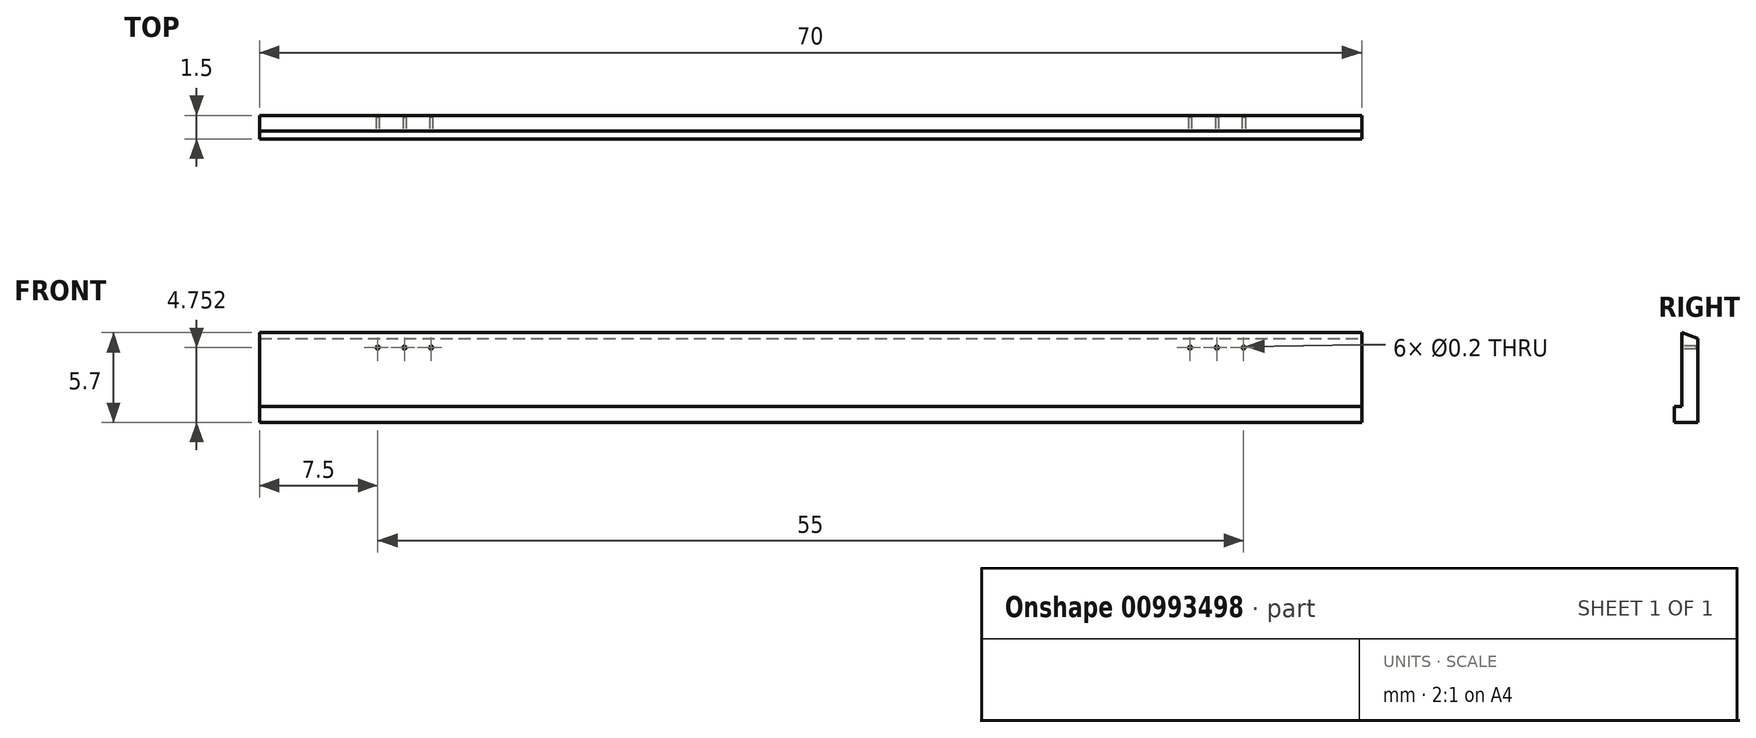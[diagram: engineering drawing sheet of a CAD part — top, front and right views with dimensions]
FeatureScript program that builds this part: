
annotation { "Feature Type Name" : "Feature", "Feature Type Description" : "" }
export const myFeature = defineFeature(function(context is Context, id is Id, definition is map)
    precondition{}
    {
        {
            var Q0;
            Q0=qCreatedBy(makeId("Right.planeOp"),FACE);
            var sketch = newSketch(context, id + "F0", { "sketchPlane" : qUnion([Q0])});
            skLineSegment(sketch, "E0", {"start": v(-40.56, -13.83) * mm, "end": v(-40.56, -18.53) * mm});
            skLineSegment(sketch, "E1", {"start": v(-40.56, -18.53) * mm, "end": v(-41.06, -18.53) * mm});
            skLineSegment(sketch, "E2", {"start": v(-41.06, -18.53) * mm, "end": v(-41.06, -19.53) * mm});
            skLineSegment(sketch, "E3", {"start": v(-41.06, -19.53) * mm, "end": v(-39.56, -19.53) * mm});
            skLineSegment(sketch, "E4", {"start": v(-39.56, -19.53) * mm, "end": v(-39.56, -13.83) * mm});
            skLineSegment(sketch, "E5", {"start": v(-39.56, -13.83) * mm, "end": v(-40.56, -13.83) * mm});
            skSolve(sketch);
        }
        {
            var Q0;
            Q0=makeQuery(id+"F0.imprint","IMPRINT",FACE,{"disambiguationData":[TD([[makeQuery(id+"F0.imprint","IMPRINT",EDGE,{"derivedFrom":sQuery(id+"F0.wireOp",EDGE,"E0")}),1.0]])]});
            extrude(context, id + "F1", {"entities" : qUnion([Q0]), "oppositeDirection" : true, "depth" : 70 * mm, "offsetDistance" : 25 * mm});
        }
        {
            var Q0;
            Q0=makeQuery(id+"F1.opExtrude","SWEPT_EDGE",EDGE,{"disambiguationData":[OSD([sQuery(id+"F0.wireOp",EDGE,"E4"),sQuery(id+"F0.wireOp",EDGE,"E5")])]});
            chamfer(context, id + "F2", {"entities" : qUnion([Q0]), "chamferType" : ChamferType.OFFSET_ANGLE, "width" : 1 * mm, "oppositeDirection" : true, "angle" : 20 * degree, "tangentPropagation" : true});
        }
        {
            var Q0;
            Q0=makeQuery(id+"F1.opExtrude","SWEPT_FACE",FACE,{"disambiguationData":[OSD([sQuery(id+"F0.wireOp",EDGE,"E0")])]});
            var sketch = newSketch(context, id + "F3", { "sketchPlane" : qUnion([Q0])});
            skLineSegment(sketch, "E6", {"start": v(-70, -13.83) * mm, "end": v(-70, -14.78) * mm});
            skLineSegment(sketch, "E7", {"start": v(-70, -14.78) * mm, "end": v(16.32, -14.78) * mm});
            skPoint(sketch, "E8", {"position": v(-62.5, -14.78) * mm});
            skPoint(sketch, "E9", {"position": v(-60.8, -14.78) * mm});
            skPoint(sketch, "E10", {"position": v(-59.1, -14.78) * mm});
            skPoint(sketch, "E11", {"position": v(-7.5, -14.78) * mm});
            skPoint(sketch, "E12", {"position": v(-9.2, -14.78) * mm});
            skPoint(sketch, "E13", {"position": v(-10.9, -14.78) * mm});
            skSolve(sketch);
        }
        {
            var Q0;
            Q0=sQuery(id+"F3.wireOp",VERTEX,"E8");
            var Q1;
            Q1=sQuery(id+"F3.wireOp",VERTEX,"E9");
            var Q2;
            Q2=sQuery(id+"F3.wireOp",VERTEX,"E10");
            var Q3;
            Q3=sQuery(id+"F3.wireOp",VERTEX,"E13");
            var Q4;
            Q4=sQuery(id+"F3.wireOp",VERTEX,"E12");
            var Q5;
            Q5=sQuery(id+"F3.wireOp",VERTEX,"E11");
            var Q6;
            Q6=makeQuery(id+"F1.opExtrude","SWEPT_BODY",BODY,{"disambiguationData":[OSD([sQuery(id+"F0.wireOp",EDGE,"E0"),sQuery(id+"F0.wireOp",EDGE,"E1"),sQuery(id+"F0.wireOp",EDGE,"E2"),sQuery(id+"F0.wireOp",EDGE,"E3"),sQuery(id+"F0.wireOp",EDGE,"E4"),sQuery(id+"F0.wireOp",EDGE,"E5")])]});
            hole(context, id + "F4", {"style" : HoleStyle.SIMPLE, "endStyle" : HoleEndStyle.BLIND, "holeDiameter" : 0.2 * mm, "majorDiameter" : 5 * mm, "holeDepth" : 0.9 * mm, "isTappedThrough" : true, "tappedDepth" : 12 * mm, "tapClearance" : 3, "locations" : qUnion([Q0, Q1, Q2, Q3, Q4, Q5]), "scope" : qUnion([Q6])});
        }
    });
